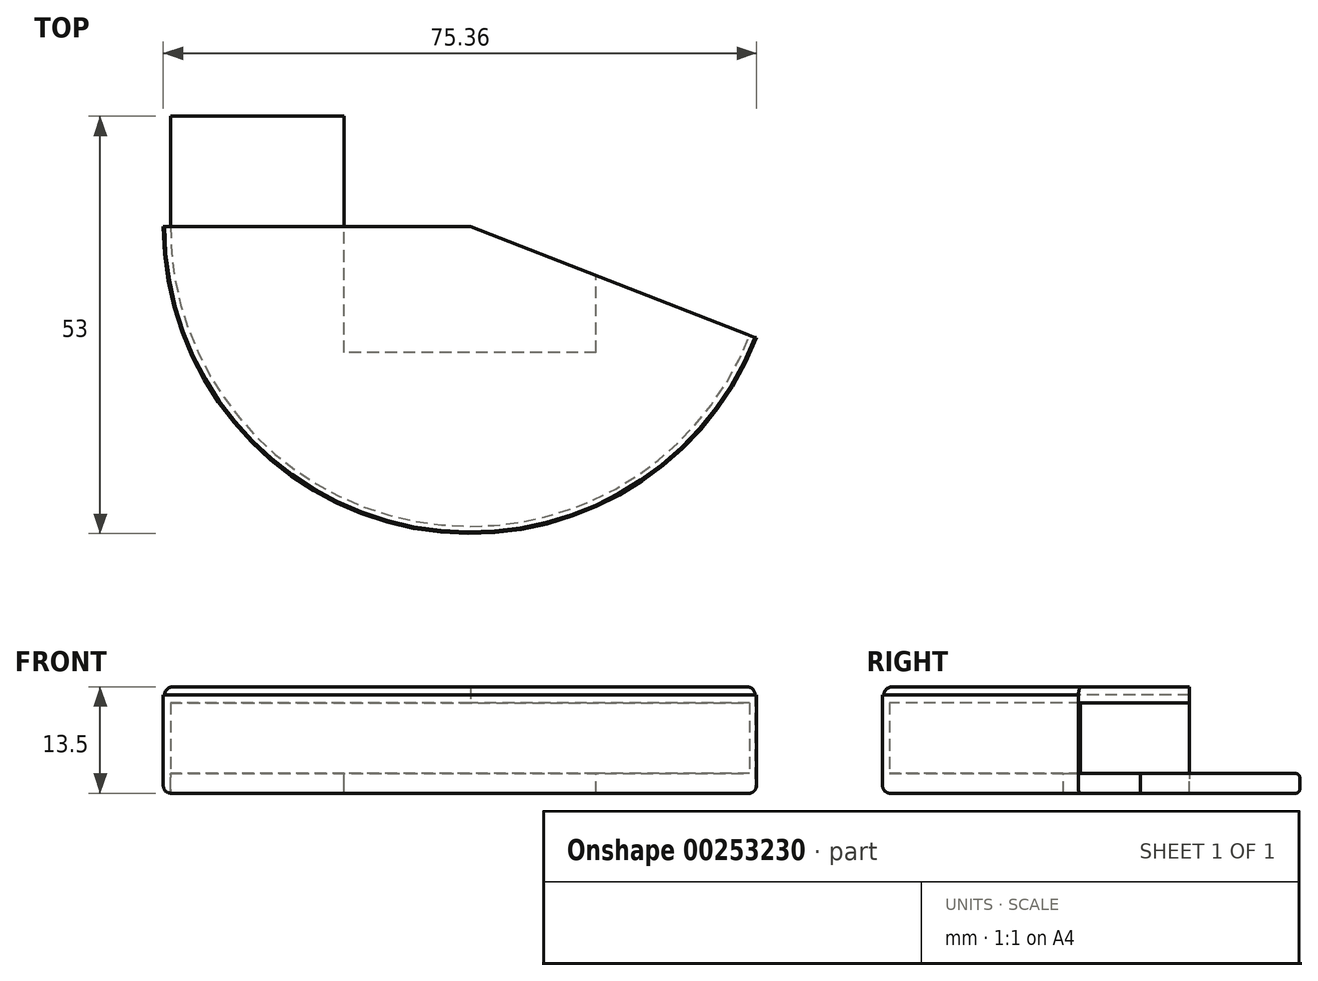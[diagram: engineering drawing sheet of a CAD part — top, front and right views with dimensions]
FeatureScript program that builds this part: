
annotation { "Feature Type Name" : "Feature", "Feature Type Description" : "" }
export const myFeature = defineFeature(function(context is Context, id is Id, definition is map)
    precondition{}
    {
        {
            var Q0;
            Q0=qCreatedBy(makeId("Top.planeOp"),FACE);
            var sketch = newSketch(context, id + "F0", { "sketchPlane" : qUnion([Q0])});
            skLineSegment(sketch, "E0.bottom", {"start": v(16, -16) * mm, "end": v(-16, -16) * mm});
            skLineSegment(sketch, "E0.top", {"start": v(16, 16) * mm, "end": v(-16, 16) * mm});
            skLineSegment(sketch, "E0.left", {"start": v(16, -16) * mm, "end": v(16, 16) * mm});
            skLineSegment(sketch, "E0.right", {"start": v(-16, -16) * mm, "end": v(-16, 16) * mm});
            skPoint(sketch, "E0.middle", {"position": v(0, 0) * mm});
            skCircle(sketch, "E1", {"center": v(0, 0) * mm, "radius": 38.1 * mm});
            skCircle(sketch, "E2", {"center": v(0, 0) * mm, "radius": 39 * mm});
            skSolve(sketch);
        }
        {
            var Q0;
            Q0 = qSketchRegion(id + "F0", true);
            extrude(context, id + "F1", {"entities" : qUnion([Q0]), "depth" : 9 * mm});
        }
        {
            var Q0;
            Q0 = qSketchRegion(id + "F0", true);
            extrude(context, id + "F2", {"entities" : qUnion([Q0]), "operationType" : NewBodyOperationType.ADD, "depth" : 10 * mm});
        }
        {
            var Q0;
            Q0=makeQuery(id+"F0.imprint","IMPRINT",FACE,{"disambiguationData":[TD([[makeQuery(id+"F0.imprint","IMPRINT",EDGE,{"derivedFrom":sQuery(id+"F0.wireOp",EDGE,"E0.bottom")}),1.0]])]});
            extrude(context, id + "F3", {"entities" : qUnion([Q0]), "oppositeDirection" : true, "depth" : 2.5 * mm});
        }
        {
            var Q0;
            Q0=qCreatedBy(makeId("Top.planeOp"),FACE);
            cPlane(context, id + "F4", {"entities" : qUnion([Q0]), "cplaneType" : CPlaneType.OFFSET, "offset" : 9 * mm, "width" : 150 * mm, "height" : 150 * mm});
        }
        {
            var Q0;
            Q0=qCreatedBy(id+"F4.planeOp",FACE);
            var sketch = newSketch(context, id + "F5", { "sketchPlane" : qUnion([Q0])});
            skCircle(sketch, "E3", {"center": v(0, 0) * mm, "radius": 38.83 * mm});
            skSolve(sketch);
        }
        {
            var Q0;
            Q0 = qSketchRegion(id + "F5", true);
            extrude(context, id + "F6", {"entities" : qUnion([Q0]), "operationType" : NewBodyOperationType.ADD, "depth" : 2 * mm});
        }
        {
            var Q0;
            Q0=makeQuery(id+"F6.opExtrude","CAP_EDGE",EDGE,{"disambiguationData":[OSD([sQuery(id+"F5.wireOp",EDGE,"E3")])],"isStart":false});
            fillet(context, id + "F7", {"entities" : qUnion([Q0]), "radius" : 1 * mm, "tangentPropagation" : true, "allowEdgeOverflow" : false});
        }
        {
            var Q0;
            Q0=qCreatedBy(makeId("Top.planeOp"),FACE);
            var sketch = newSketch(context, id + "F8", { "sketchPlane" : qUnion([Q0])});
            skLineSegment(sketch, "E4", {"start": v(-42, 0) * mm, "end": v(0, 0) * mm});
            skLineSegment(sketch, "E5", {"start": v(49.3, 48) * mm, "end": v(-41.2, 48) * mm});
            skLineSegment(sketch, "E6", {"start": v(-41.2, 48) * mm, "end": v(-42, 0) * mm});
            skLineSegment(sketch, "E7", {"start": v(0, 0) * mm, "end": v(36.19, -14.12) * mm});
            skLineSegment(sketch, "E8", {"start": v(36.19, -14.12) * mm, "end": v(49.78, -14.12) * mm});
            skLineSegment(sketch, "E9", {"start": v(49.78, -14.12) * mm, "end": v(49.3, 48) * mm});
            skSolve(sketch);
        }
        {
            var Q0;
            Q0 = qSketchRegion(id + "F8", true);
            extrude(context, id + "F9", {"entities" : qUnion([Q0]), "endBound" : BoundingType.SYMMETRIC, "depth" : 25 * mm});
        }
        {
            var Q0;
            Q0 = qSketchRegion(id + "F8", true);
            extrude(context, id + "F10", {"entities" : qUnion([Q0]), "operationType" : NewBodyOperationType.REMOVE, "endBound" : BoundingType.SYMMETRIC, "depth" : 25 * mm});
        }
        {
            var Q0;
            Q0=makeQuery(id+"F1.opExtrude","CAP_FACE",FACE,{"disambiguationData":[OSD([sQuery(id+"F0.wireOp",EDGE,"E1"),sQuery(id+"F0.wireOp",EDGE,"E2")])],"isStart":true});
            extrude(context, id + "F11", {"entities" : qUnion([Q0]), "depth" : 2.5 * mm});
        }
        {
            var Q0;
            Q0=makeQuery(id+"F11.opExtrude","CAP_EDGE",EDGE,{"disambiguationData":[OSD([sQuery(id+"F0.wireOp",EDGE,"E2")])],"isStart":false});
            fillet(context, id + "F12", {"entities" : qUnion([Q0]), "radius" : 1 * mm, "tangentPropagation" : true, "allowEdgeOverflow" : false});
        }
        {
            var Q0;
            {var subQ1=sQuery(id+"F0.wireOp",EDGE,"E0.right");Q0=makeQuery(id+"F10.boolean.opBoolean","COPY",FACE,{"disambiguationData":[TD([makeQuery(id+"F3.opExtrude","SWEPT_FACE",FACE,{"disambiguationData":[OSD([subQ1])]})])],"derivedFrom":makeQuery(id+"F10.opExtrude","SWEPT_FACE",FACE,{"disambiguationData":[OSD([sQuery(id+"F8.wireOp",EDGE,"E4")])]})});}
            extrude(context, id + "F13", {"entities" : qUnion([Q0]), "operationType" : NewBodyOperationType.ADD, "depth" : 14 * mm});
        }
        {
            var Q0;
            {var subQ0=sQuery(id+"F8.wireOp",EDGE,"E4");var subQ1=sQuery(id+"F0.wireOp",EDGE,"E1");var subQ2=sQuery(id+"F0.wireOp",EDGE,"E0.right");var subQ3=sQuery(id+"F0.wireOp",EDGE,"E0.left");var subQ4=sQuery(id+"F0.wireOp",EDGE,"E0.top");var subQ5=sQuery(id+"F0.wireOp",EDGE,"E0.bottom");Q0=makeQuery(id+"F13.opExtrude","CAP_EDGE",EDGE,{"disambiguationData":[OSD([subQ5,subQ4,subQ3,subQ2,subQ1,subQ0]),TDD([makeQuery(id+"F10.boolean.opBoolean","INTERSECT",EDGE,{"derivedFrom":[makeQuery(id+"F3.opExtrude","CAP_FACE",FACE,{"disambiguationData":[OSD([subQ5,subQ4,subQ3,subQ2,subQ1])],"isStart":false}),makeQuery(id+"F10.opExtrude","SWEPT_FACE",FACE,{"disambiguationData":[OSD([subQ0])]})]})])],"isStart":false});}
            var Q1;
            {var subQ0=sQuery(id+"F8.wireOp",EDGE,"E4");var subQ1=sQuery(id+"F0.wireOp",EDGE,"E1");var subQ2=sQuery(id+"F0.wireOp",EDGE,"E0.right");var subQ3=sQuery(id+"F0.wireOp",EDGE,"E0.left");var subQ4=sQuery(id+"F0.wireOp",EDGE,"E0.top");var subQ5=sQuery(id+"F0.wireOp",EDGE,"E0.bottom");Q1=makeQuery(id+"F13.opExtrude","CAP_EDGE",EDGE,{"disambiguationData":[OSD([subQ5,subQ4,subQ3,subQ2,subQ1,subQ0]),TDD([makeQuery(id+"F10.boolean.opBoolean","INTERSECT",EDGE,{"derivedFrom":[makeQuery(id+"F3.opExtrude","CAP_FACE",FACE,{"disambiguationData":[OSD([subQ5,subQ4,subQ3,subQ2,subQ1])],"isStart":true}),makeQuery(id+"F10.opExtrude","SWEPT_FACE",FACE,{"disambiguationData":[OSD([subQ0])]})]})])],"isStart":false});}
            fillet(context, id + "F14", {"entities" : qUnion([Q0, Q1]), "radius" : .5 * mm, "tangentPropagation" : true, "allowEdgeOverflow" : false});
        }
    });
